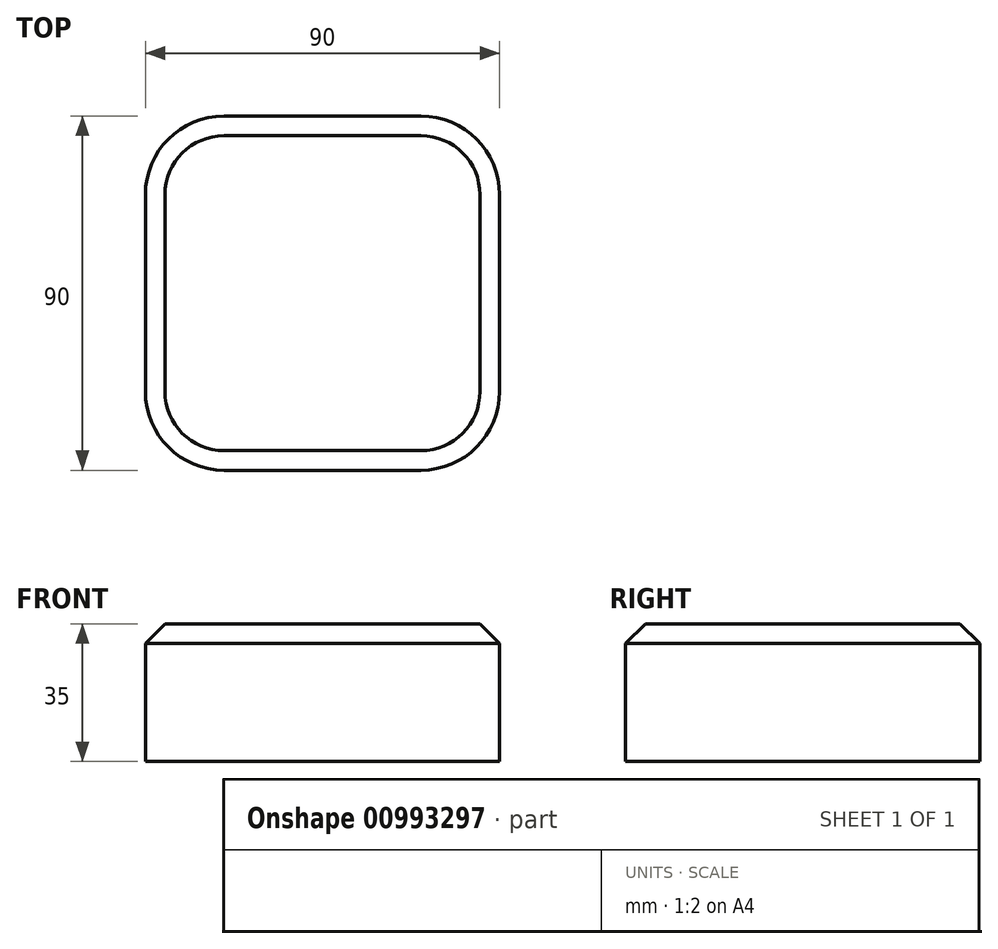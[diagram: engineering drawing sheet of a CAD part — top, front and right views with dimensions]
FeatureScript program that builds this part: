
annotation { "Feature Type Name" : "Feature", "Feature Type Description" : "" }
export const myFeature = defineFeature(function(context is Context, id is Id, definition is map)
    precondition{}
    {
        {
            var Q0;
            Q0=qCreatedBy(makeId("Top.planeOp"),FACE);
            var sketch = newSketch(context, id + "F0", { "sketchPlane" : qUnion([Q0])});
            skLineSegment(sketch, "E0.bottom", {"start": v(38.64, 39.46) * mm, "end": v(88.64, 39.46) * mm});
            skLineSegment(sketch, "E0.top", {"start": v(38.64, -50.54) * mm, "end": v(88.64, -50.54) * mm});
            skLineSegment(sketch, "E0.left", {"start": v(18.64, 19.46) * mm, "end": v(18.64, -30.54) * mm});
            skLineSegment(sketch, "E0.right", {"start": v(108.64, 19.46) * mm, "end": v(108.64, -30.54) * mm});
            skPoint(sketch, "E1.visualSharp", {"position": v(18.64, 39.46) * mm});
            skArc(sketch, "E1.filletArc", {"start": v(38.64, 39.46) * mm, "mid": v(24.5, 33.6) * mm, "end": v(18.64, 19.46) * mm});
            skPoint(sketch, "E2.visualSharp", {"position": v(18.64, -50.54) * mm});
            skArc(sketch, "E2.filletArc", {"start": v(18.64, -30.54) * mm, "mid": v(24.5, -44.68) * mm, "end": v(38.64, -50.54) * mm});
            skPoint(sketch, "E3.visualSharp", {"position": v(108.64, -50.54) * mm});
            skArc(sketch, "E3.filletArc", {"start": v(88.64, -50.54) * mm, "mid": v(102.78, -44.68) * mm, "end": v(108.64, -30.54) * mm});
            skPoint(sketch, "E4.visualSharp", {"position": v(108.64, 39.46) * mm});
            skArc(sketch, "E4.filletArc", {"start": v(108.64, 19.46) * mm, "mid": v(102.78, 33.6) * mm, "end": v(88.64, 39.46) * mm});
            skSolve(sketch);
        }
        {
            var Q0;
            Q0 = qSketchRegion(id + "F0", true);
            extrude(context, id + "F1", {"entities" : qUnion([Q0]), "depth" : 35 * mm, "offsetDistance" : 25 * mm});
        }
        {
            var Q0;
            Q0=makeQuery(id+"F1.opExtrude","CAP_EDGE",EDGE,{"disambiguationData":[OSD([sQuery(id+"F0.wireOp",EDGE,"E0.left")])],"isStart":false});
            chamfer(context, id + "F2", {"entities" : qUnion([Q0]), "width" : 5 * mm, "tangentPropagation" : true});
        }
    });
